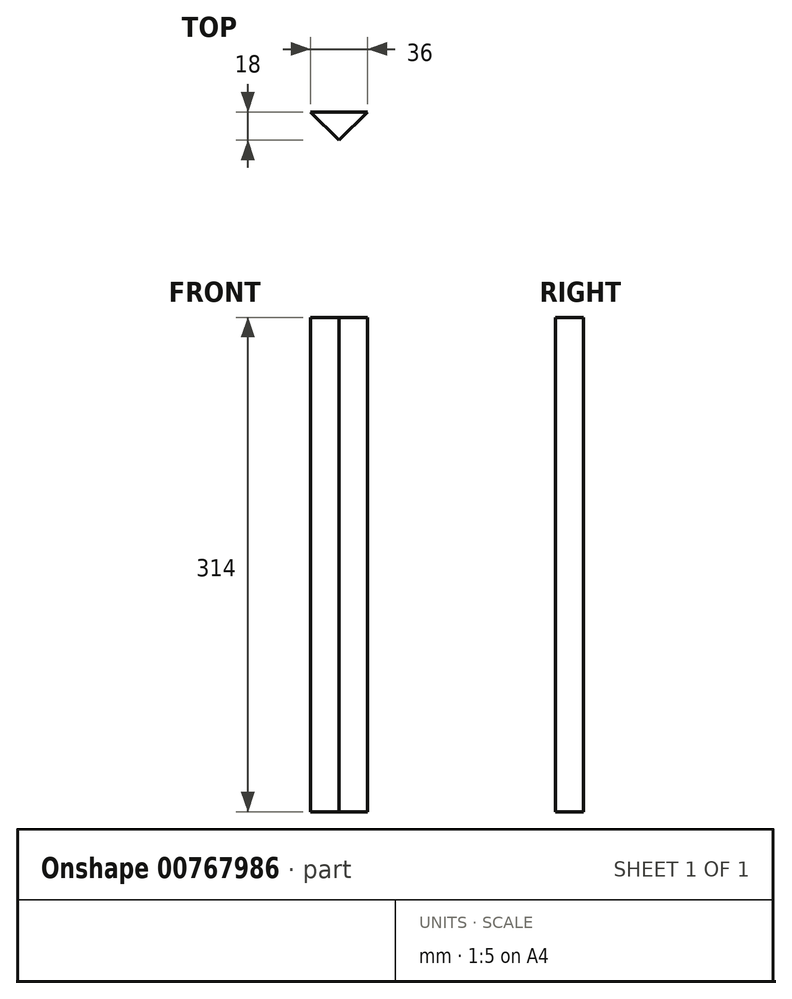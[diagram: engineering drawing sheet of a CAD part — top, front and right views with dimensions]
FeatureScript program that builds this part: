
annotation { "Feature Type Name" : "Feature", "Feature Type Description" : "" }
export const myFeature = defineFeature(function(context is Context, id is Id, definition is map)
    precondition{}
    {
        {
            var Q0;
            Q0=qCreatedBy(makeId("Front.planeOp"),FACE);
            var sketch = newSketch(context, id + "F0", { "sketchPlane" : qUnion([Q0])});
            skLineSegment(sketch, "E0.bottom", {"start": v(18, 157) * mm, "end": v(-18, 157) * mm});
            skLineSegment(sketch, "E0.top", {"start": v(18, -157) * mm, "end": v(-18, -157) * mm});
            skLineSegment(sketch, "E0.left", {"start": v(18, 157) * mm, "end": v(18, -157) * mm});
            skLineSegment(sketch, "E0.right", {"start": v(-18, 157) * mm, "end": v(-18, -157) * mm});
            skPoint(sketch, "E0.middle", {"position": v(0, 0) * mm});
            skSolve(sketch);
        }
        {
            var Q0;
            Q0 = qSketchRegion(id + "F0", true);
            extrude(context, id + "F1", {"entities" : qUnion([Q0]), "depth" : 18 * mm, "offsetDistance" : 25 * mm});
        }
        {
            var Q0;
            Q0=makeQuery(id+"F1.opExtrude","CAP_EDGE",EDGE,{"disambiguationData":[OSD([sQuery(id+"F0.wireOp",EDGE,"E0.right")])],"isStart":false});
            var Q1;
            Q1=makeQuery(id+"F1.opExtrude","CAP_EDGE",EDGE,{"disambiguationData":[OSD([sQuery(id+"F0.wireOp",EDGE,"E0.left")])],"isStart":false});
            chamfer(context, id + "F2", {"entities" : qUnion([Q0, Q1]), "width" : 18 * mm, "tangentPropagation" : true});
        }
    });
